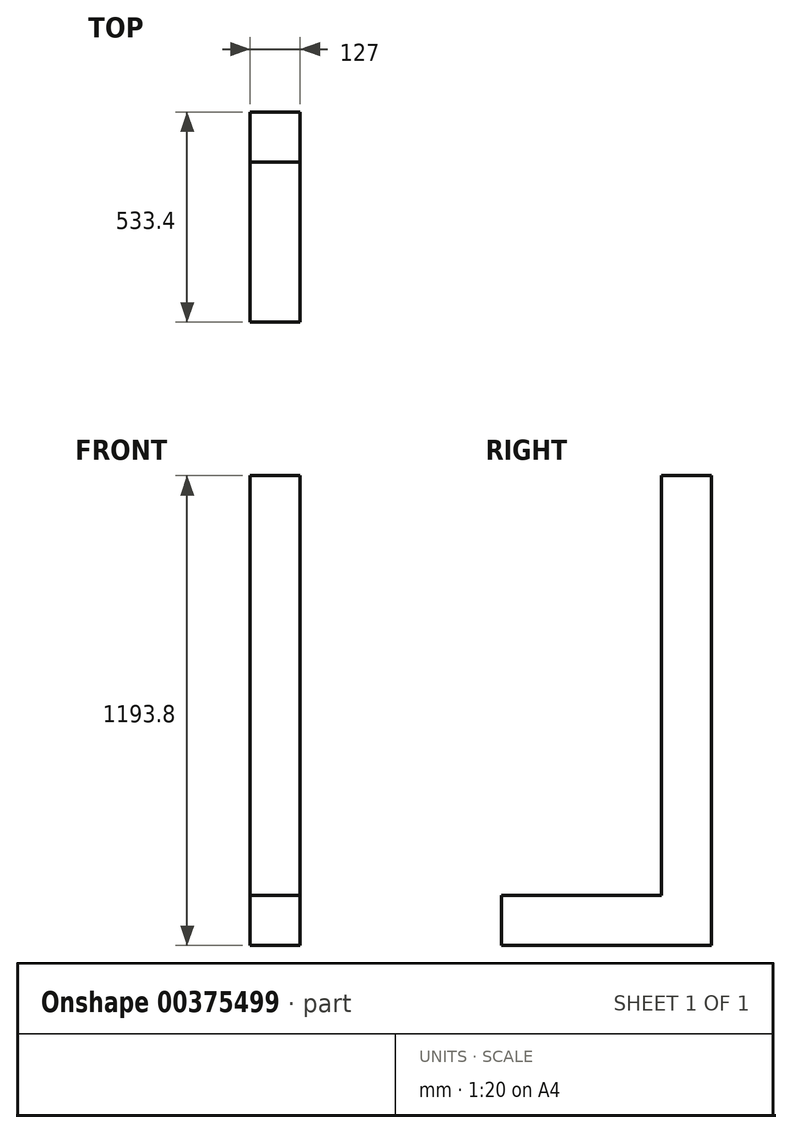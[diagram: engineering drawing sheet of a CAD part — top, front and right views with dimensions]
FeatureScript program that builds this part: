
annotation { "Feature Type Name" : "Feature", "Feature Type Description" : "" }
export const myFeature = defineFeature(function(context is Context, id is Id, definition is map)
    precondition{}
    {
        {
            var Q0;
            Q0=qCreatedBy(makeId("Front.planeOp"),FACE);
            var sketch = newSketch(context, id + "F0", { "sketchPlane" : qUnion([Q0])});
            skLineSegment(sketch, "E0.bottom", {"start": v(63.5, 63.5) * mm, "end": v(-63.5, 63.5) * mm});
            skLineSegment(sketch, "E0.top", {"start": v(63.5, -63.5) * mm, "end": v(-63.5, -63.5) * mm});
            skLineSegment(sketch, "E0.left", {"start": v(63.5, 63.5) * mm, "end": v(63.5, -63.5) * mm});
            skLineSegment(sketch, "E0.right", {"start": v(-63.5, 63.5) * mm, "end": v(-63.5, -63.5) * mm});
            skPoint(sketch, "E0.middle", {"position": v(0, 0) * mm});
            skSolve(sketch);
        }
        {
            var Q0;
            Q0=makeQuery(id+"F0.imprint","IMPRINT",FACE,{"disambiguationData":[TD([[makeQuery(id+"F0.imprint","IMPRINT",EDGE,{"derivedFrom":sQuery(id+"F0.wireOp",EDGE,"E0.bottom")}),1.0]])]});
            extrude(context, id + "F1", {"entities" : qUnion([Q0]), "depth" : 533.4 * mm});
        }
        {
            var Q0;
            Q0=makeQuery(id+"F1.opExtrude","SWEPT_FACE",FACE,{"disambiguationData":[OSD([sQuery(id+"F0.wireOp",EDGE,"E0.top")])]});
            var sketch = newSketch(context, id + "F2", { "sketchPlane" : qUnion([Q0])});
            skLineSegment(sketch, "E1.bottom", {"start": v(-63.5, 0) * mm, "end": v(63.5, 0) * mm});
            skLineSegment(sketch, "E1.top", {"start": v(-63.5, 127) * mm, "end": v(63.5, 127) * mm});
            skLineSegment(sketch, "E1.left", {"start": v(-63.5, 0) * mm, "end": v(-63.5, 127) * mm});
            skLineSegment(sketch, "E1.right", {"start": v(63.5, 0) * mm, "end": v(63.5, 127) * mm});
            skSolve(sketch);
        }
        {
            var Q0;
            Q0=makeQuery(id+"F2.imprint","IMPRINT",FACE,{"disambiguationData":[TD([[makeQuery(id+"F2.imprint","IMPRINT",EDGE,{"derivedFrom":sQuery(id+"F2.wireOp",EDGE,"E1.bottom")}),-1.0]])]});
            extrude(context, id + "F3", {"entities" : qUnion([Q0]), "operationType" : NewBodyOperationType.ADD, "oppositeDirection" : true, "depth" : 1193.8 * mm});
        }
    });
